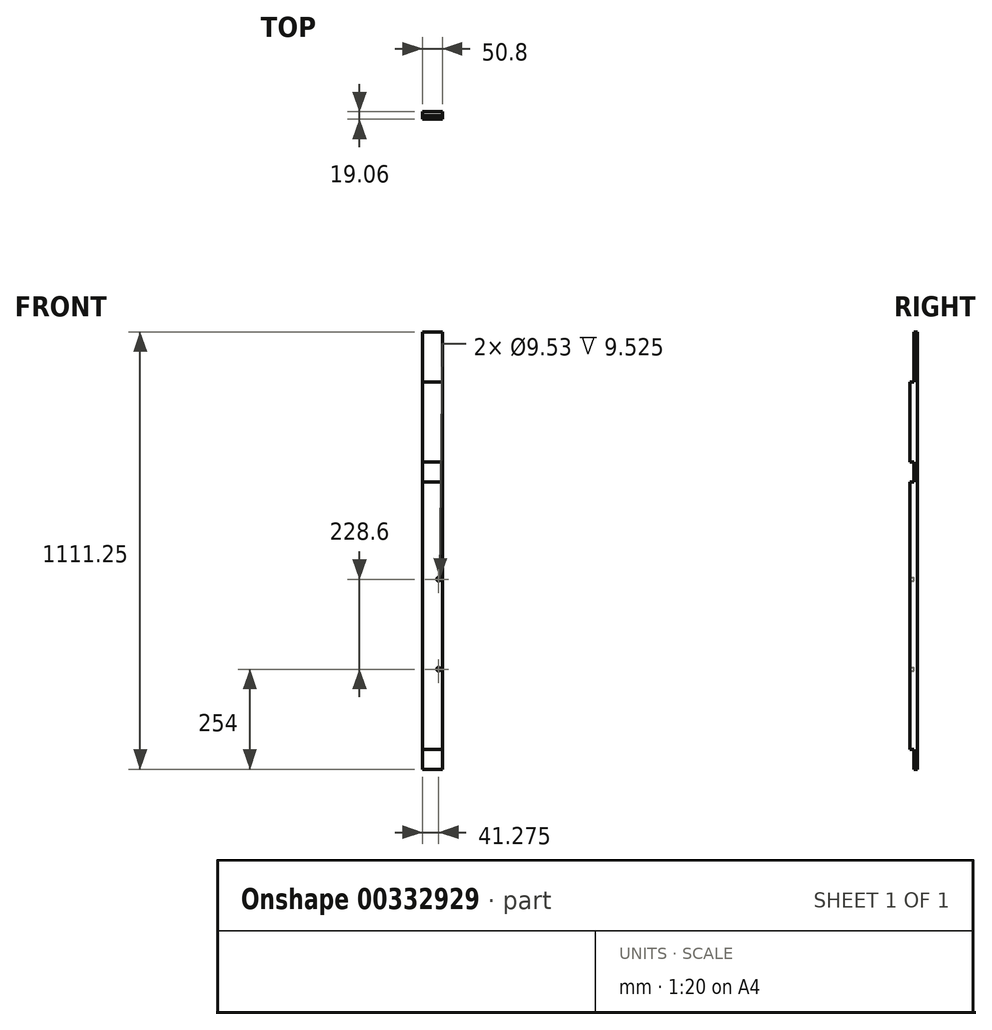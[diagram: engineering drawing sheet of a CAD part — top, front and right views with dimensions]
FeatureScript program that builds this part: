
annotation { "Feature Type Name" : "Feature", "Feature Type Description" : "" }
export const myFeature = defineFeature(function(context is Context, id is Id, definition is map)
    precondition{}
    {
        {
            var Q0;
            Q0=qCreatedBy(makeId("Top.planeOp"),FACE);
            var sketch = newSketch(context, id + "F0", { "sketchPlane" : qUnion([Q0])});
            skLineSegment(sketch, "E0.bottom", {"start": v(25.4, 9.53) * mm, "end": v(-25.4, 9.53) * mm});
            skLineSegment(sketch, "E0.top", {"start": v(25.4, -9.53) * mm, "end": v(-25.4, -9.53) * mm});
            skLineSegment(sketch, "E0.left", {"start": v(25.4, 9.53) * mm, "end": v(25.4, -9.52) * mm});
            skLineSegment(sketch, "E0.right", {"start": v(-25.4, 9.53) * mm, "end": v(-25.4, -9.53) * mm});
            skPoint(sketch, "E0.middle", {"position": v(0, 0) * mm});
            skSolve(sketch);
        }
        {
            var Q0;
            Q0=makeQuery(id+"F0.imprint","IMPRINT",FACE,{"disambiguationData":[TD([[makeQuery(id+"F0.imprint","IMPRINT",EDGE,{"derivedFrom":sQuery(id+"F0.wireOp",EDGE,"E0.bottom")}),1.0]])]});
            extrude(context, id + "F1", {"entities" : qUnion([Q0]), "depth" : 1111.25 * mm});
        }
        {
            var Q0;
            Q0=qCreatedBy(makeId("Front.planeOp"),FACE);
            var sketch = newSketch(context, id + "F2", { "sketchPlane" : qUnion([Q0])});
            skLineSegment(sketch, "E1.bottom", {"start": v(-38.77, 0) * mm, "end": v(83.66, 0) * mm});
            skLineSegment(sketch, "E1.top", {"start": v(-38.77, 50.8) * mm, "end": v(83.66, 50.8) * mm});
            skLineSegment(sketch, "E1.left", {"start": v(-38.77, 0) * mm, "end": v(-38.77, 50.8) * mm});
            skLineSegment(sketch, "E1.right", {"start": v(83.66, 0) * mm, "end": v(83.66, 50.8) * mm});
            skLineSegment(sketch, "E2.bottom", {"start": v(-44.21, 730.25) * mm, "end": v(49.65, 730.25) * mm});
            skLineSegment(sketch, "E2.top", {"start": v(-44.21, 781.05) * mm, "end": v(49.65, 781.05) * mm});
            skLineSegment(sketch, "E2.left", {"start": v(-44.21, 730.25) * mm, "end": v(-44.21, 781.05) * mm});
            skLineSegment(sketch, "E2.right", {"start": v(49.65, 730.25) * mm, "end": v(49.65, 781.05) * mm});
            skLineSegment(sketch, "E3.bottom", {"start": v(-210.36, 984.25) * mm, "end": v(132.8, 984.25) * mm});
            skLineSegment(sketch, "E3.top", {"start": v(-210.36, 1111.25) * mm, "end": v(132.8, 1111.25) * mm});
            skLineSegment(sketch, "E3.left", {"start": v(-210.36, 984.25) * mm, "end": v(-210.36, 1111.25) * mm});
            skLineSegment(sketch, "E3.right", {"start": v(132.8, 984.25) * mm, "end": v(132.8, 1111.25) * mm});
            skSolve(sketch);
        }
        {
            var Q0;
            Q0=qSketchRegion(id+"F2",true);
            extrude(context, id + "F3", {"entities" : qUnion([Q0]), "operationType" : NewBodyOperationType.REMOVE, "depth" : 25.4 * mm});
        }
        {
            var Q0;
            Q0=qCreatedBy(makeId("Front.planeOp"),FACE);
            var sketch = newSketch(context, id + "F4", { "sketchPlane" : qUnion([Q0])});
            skCircle(sketch, "E4", {"center": v(15.88, 254) * mm, "radius": 4.76 * mm});
            skCircle(sketch, "E5", {"center": v(15.87, 482.6) * mm, "radius": 4.76 * mm});
            skSolve(sketch);
        }
        {
            var Q0;
            Q0=qSketchRegion(id+"F4",true);
            extrude(context, id + "F5", {"entities" : qUnion([Q0]), "operationType" : NewBodyOperationType.REMOVE, "depth" : 25.4 * mm});
        }
    });
